AUTODESK INVENTOR PART (.ipt)
format: ipt  version: 2014 (Build 180170000, 170)  size: 86,528 bytes
history: native  units: mm (DEFAULTED — no unit token found)
features: other x4, sketch x1, sweep x1
ambient origin geometry x8: Origin, YZ Plane, XZ Plane, XY Plane, X Axis, Y Axis, Z Axis, Center Point
bodies: Solid1 (feature_tree)
feature tree (6):
  sketch  "Sketch Path"  dims[d0=10.6172mm d1=2.682204mm d2=6.981317mm d3=7.9375mm d4=0.0mm d5=0.0mm d6=0.0mm d7=0.0mm d8=0.0mm]
  other  "Cross Section Plane"
  other  "Work Axis1"
  other  "Work Axis2"
  sweep  "Belt"
  other  "Cross Section"
